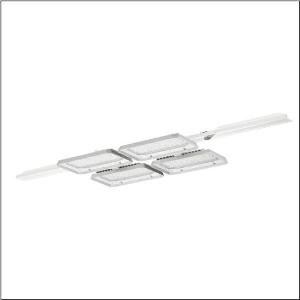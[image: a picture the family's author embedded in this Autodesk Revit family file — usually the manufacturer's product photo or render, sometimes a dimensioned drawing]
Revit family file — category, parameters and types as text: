
# Revit family: highbay_11_51hla1d24nla
name_source: partatom
category: Lighting Fixtures
units: mm (PartAtom-declared; Revit-internal decimal feet)

## family parameters
Cut with Voids When Loaded = No
Host = Face
Light Source = No
Part Type = Normal
Room Calculation Point = No
Round Connector Dimension = Use Diameter
Shared = No

## types (1)
- --- (1 x LED, 32370 lm, 189.7 W, 4000K)
    Apparent Load = 759 VA
    CIE Flux Codes = 88 95 99 100 99
    Color Rendering = 80
    Color Temperature = 4000K
    Default Elevation = 1800 mm
    Description = Highbay 11, LED high bay luminaire, end cap, primary light control with lens, of PMMA, light emission: direct distribution, primary light characteristic: symmetric, installation type: recessed, for 2x 2x LED, rated luminous flux: 32.370lm, luminous efficacy: 171lm/W, light colour: 840, colour temperature: 4000K, control gear: ECG DALI, with system connector, mains connection: 230..240V, AC, 50/60Hz, rated input power: 190W, LED unit, of diecast aluminium, unplated, bead blasted, silver, for tool-free mounting of luminaire to Licross® trunking rail, length: 1.500mm, width: 500mm, height: 65mm, housing, of diecast aluminium, uncoated, bead blasted, silver, fixing on rail side, of aluminium, anodised, metallic grey, end cap, of PC, grey, protection rating (complete): IP64, insulation class (complete): insulation class I (protective earthing), certification: CE, UKCA, protection symbol: D, impact resistance: IK08 with glass or PC cover, permissible operating ambient temperature: -35..+45°C, corresponds to IFS (International Featured Standards) requirements for safety and quality in the food industry, packaging unit: 1 piece
    Height = 105 mm
    Lamp = 1 x LED
    Lamp Light Flux = 32370 lm
    Lamp Power = 189.7 W
    Lamp count = 1
    Length = 1500 mm
    Luminous efficacy = 171 lm/W
    Manufacturer = Siteco
    ModVariant = No
    Model = 51HLA1D24NLA
    Mounting Place = Ceiling
    Mounting Type = Pendant
    Number of Poles = 1
    OnlyDefault = Yes
    Power Factor = 1
    Product Name = Highbay 11
    Product group = LED high bay luminaire
    ProductGroupID = 903
    Protection Class = Protection class I
    Protection Degree = IP 64
    RLX_Detail_Level = 1
    RLX_Emergency_Light_Flux = 0 lm
    RLX_Emergency_Type = 0
    RLX_Emergency_Type_DB = No
    RlxData = <blob elided: 88273 chars, md5=39f30342>
    Socket = socket
    Standby Power = 0 W
    System Light Flux = 129480 lm
    System Power = 759 W
    Type Comments = factory setting: luminous flux: 100 % | dim-lin: 254 | 535 mA
    Type Image = l_1004707.jpg
    URL = http://relux.com
    VarID = @adj_175679
    Voltage = 0 V
    Weight = 0.00 kg
    Width = 500 mm

## geometry (parser evidence)
native form markers: Blend x4, Sweep x18
no freeform markers — native parametric forms only
